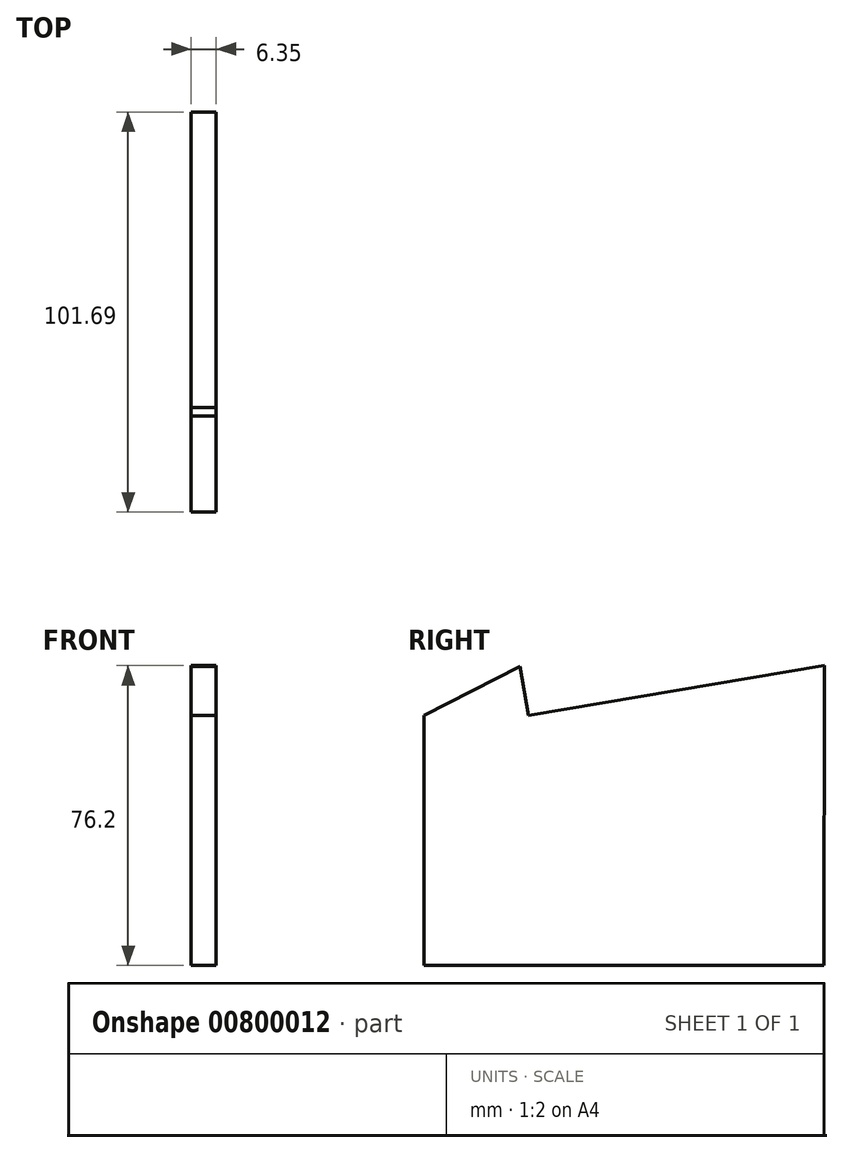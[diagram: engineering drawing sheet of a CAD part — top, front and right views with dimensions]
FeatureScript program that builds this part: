
annotation { "Feature Type Name" : "Feature", "Feature Type Description" : "" }
export const myFeature = defineFeature(function(context is Context, id is Id, definition is map)
    precondition{}
    {
        {
            var Q0;
            Q0=qCreatedBy(makeId("Right.planeOp"),FACE);
            var sketch = newSketch(context, id + "F0", { "sketchPlane" : qUnion([Q0])});
            skLineSegment(sketch, "E0", {"start": v(-16.58, 12.52) * mm, "end": v(-14.46, 0) * mm});
            skLineSegment(sketch, "E1", {"start": v(-14.46, 0) * mm, "end": v(60.67, 12.7) * mm});
            skLineSegment(sketch, "E2", {"start": v(60.58, -63.5) * mm, "end": v(-41.02, -63.5) * mm});
            skLineSegment(sketch, "E3", {"start": v(-41.02, 0) * mm, "end": v(-16.58, 12.52) * mm});
            skLineSegment(sketch, "E4", {"start": v(60.67, 12.7) * mm, "end": v(60.58, -63.5) * mm});
            skLineSegment(sketch, "E5", {"start": v(-41.02, 0) * mm, "end": v(-41.02, -63.5) * mm});
            skSolve(sketch);
        }
        {
            var Q0;
            Q0=makeQuery(id+"F0.imprint","IMPRINT",FACE,{"disambiguationData":[TD([[makeQuery(id+"F0.imprint","IMPRINT",EDGE,{"derivedFrom":sQuery(id+"F0.wireOp",EDGE,"E0")}),-1.0]])]});
            extrude(context, id + "F1", {"entities" : qUnion([Q0]), "depth" : 6.35 * mm, "offsetDistance" : 25.4 * mm});
        }
    });
